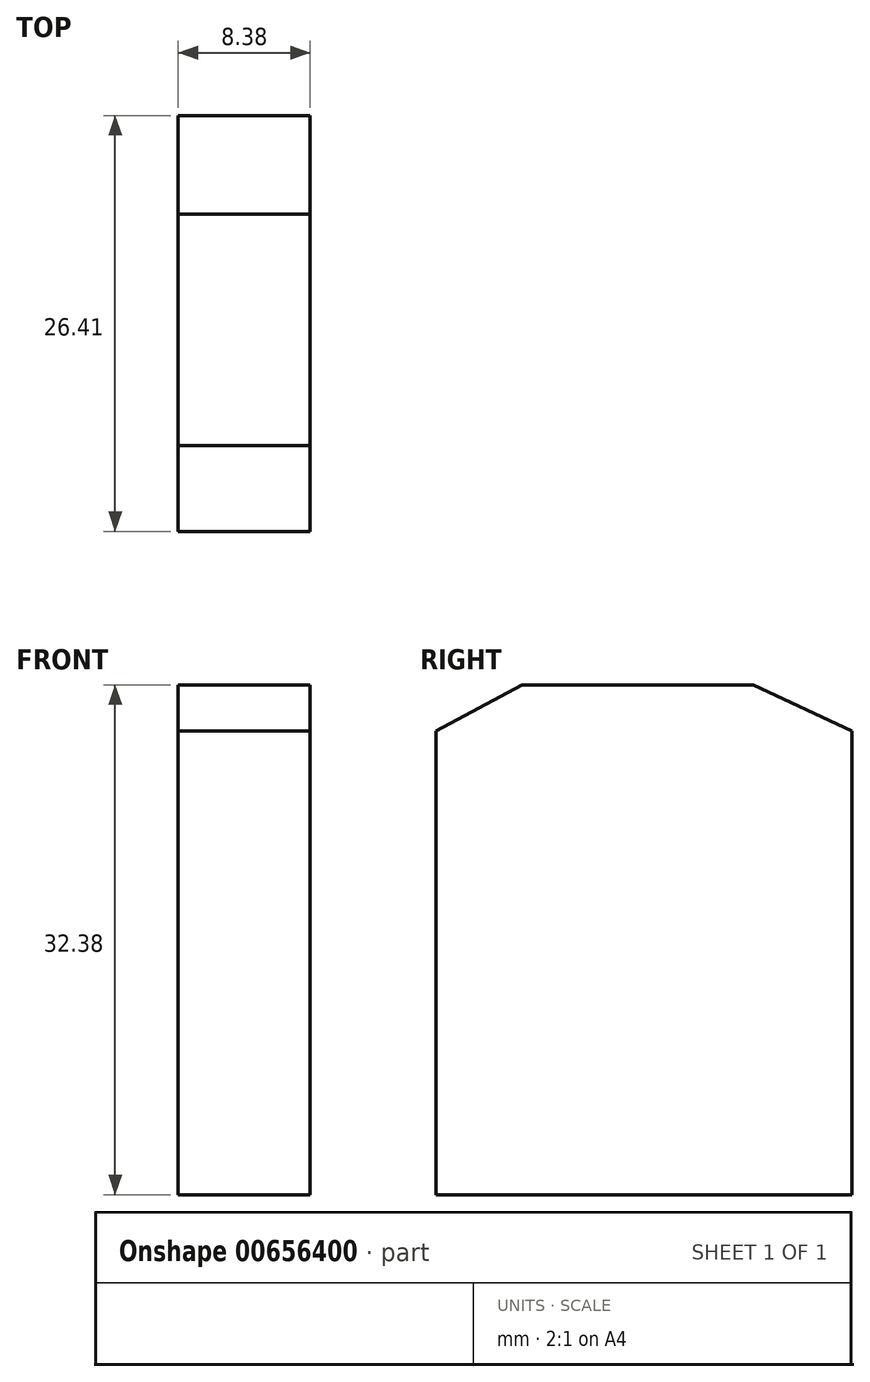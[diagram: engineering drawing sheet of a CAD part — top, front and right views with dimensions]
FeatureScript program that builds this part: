
annotation { "Feature Type Name" : "Feature", "Feature Type Description" : "" }
export const myFeature = defineFeature(function(context is Context, id is Id, definition is map)
    precondition{}
    {
        {
            var Q0;
            Q0=qCreatedBy(makeId("Right.planeOp"),FACE);
            var sketch = newSketch(context, id + "F0", { "sketchPlane" : qUnion([Q0])});
            skLineSegment(sketch, "E0", {"start": v(5.47, 32.38) * mm, "end": v(20.16, 32.38) * mm});
            skLineSegment(sketch, "E1", {"start": v(26.4, 29.44) * mm, "end": v(26.4, 0) * mm});
            skLineSegment(sketch, "E2", {"start": v(26.4, 0) * mm, "end": v(0, 0) * mm});
            skLineSegment(sketch, "E3", {"start": v(0, 0) * mm, "end": v(0, 29.44) * mm});
            skLineSegment(sketch, "E4", {"start": v(5.47, 32.38) * mm, "end": v(5.47, 0) * mm});
            skLineSegment(sketch, "E5", {"start": v(20.16, 32.38) * mm, "end": v(20.16, 0) * mm});
            skLineSegment(sketch, "E6", {"start": v(20.16, 32.38) * mm, "end": v(26.4, 29.44) * mm});
            skLineSegment(sketch, "E7", {"start": v(5.47, 32.38) * mm, "end": v(0, 29.44) * mm});
            skPoint(sketch, "E8.orphan", {"position": v(0, 32.38) * mm});
            skSolve(sketch);
        }
        {
            var Q0;
            {var subQ0=sQuery(id+"F0.wireOp",EDGE,"E1");Q0=makeQuery(id+"F0.imprint","IMPRINT",FACE,{"disambiguationData":[TD([[makeQuery(id+"F0.imprint","IMPRINT",EDGE,{"derivedFrom":subQ0}),-1.0]])]});}
            var Q1;
            {var subQ0=sQuery(id+"F0.wireOp",EDGE,"E3");Q1=makeQuery(id+"F0.imprint","IMPRINT",FACE,{"disambiguationData":[TD([[makeQuery(id+"F0.imprint","IMPRINT",EDGE,{"derivedFrom":subQ0}),-1.0]])]});}
            var Q2;
            Q2=makeQuery(id+"F0.imprint","IMPRINT",FACE,{"disambiguationData":[TD([[makeQuery(id+"F0.imprint","IMPRINT",EDGE,{"derivedFrom":sQuery(id+"F0.wireOp",EDGE,"E0")}),-1.0]])]});
            extrude(context, id + "F1", {"entities" : qUnion([Q0, Q1, Q2]), "oppositeDirection" : true, "depth" : 8.38 * mm, "offsetDistance" : 25.4 * mm});
        }
    });
